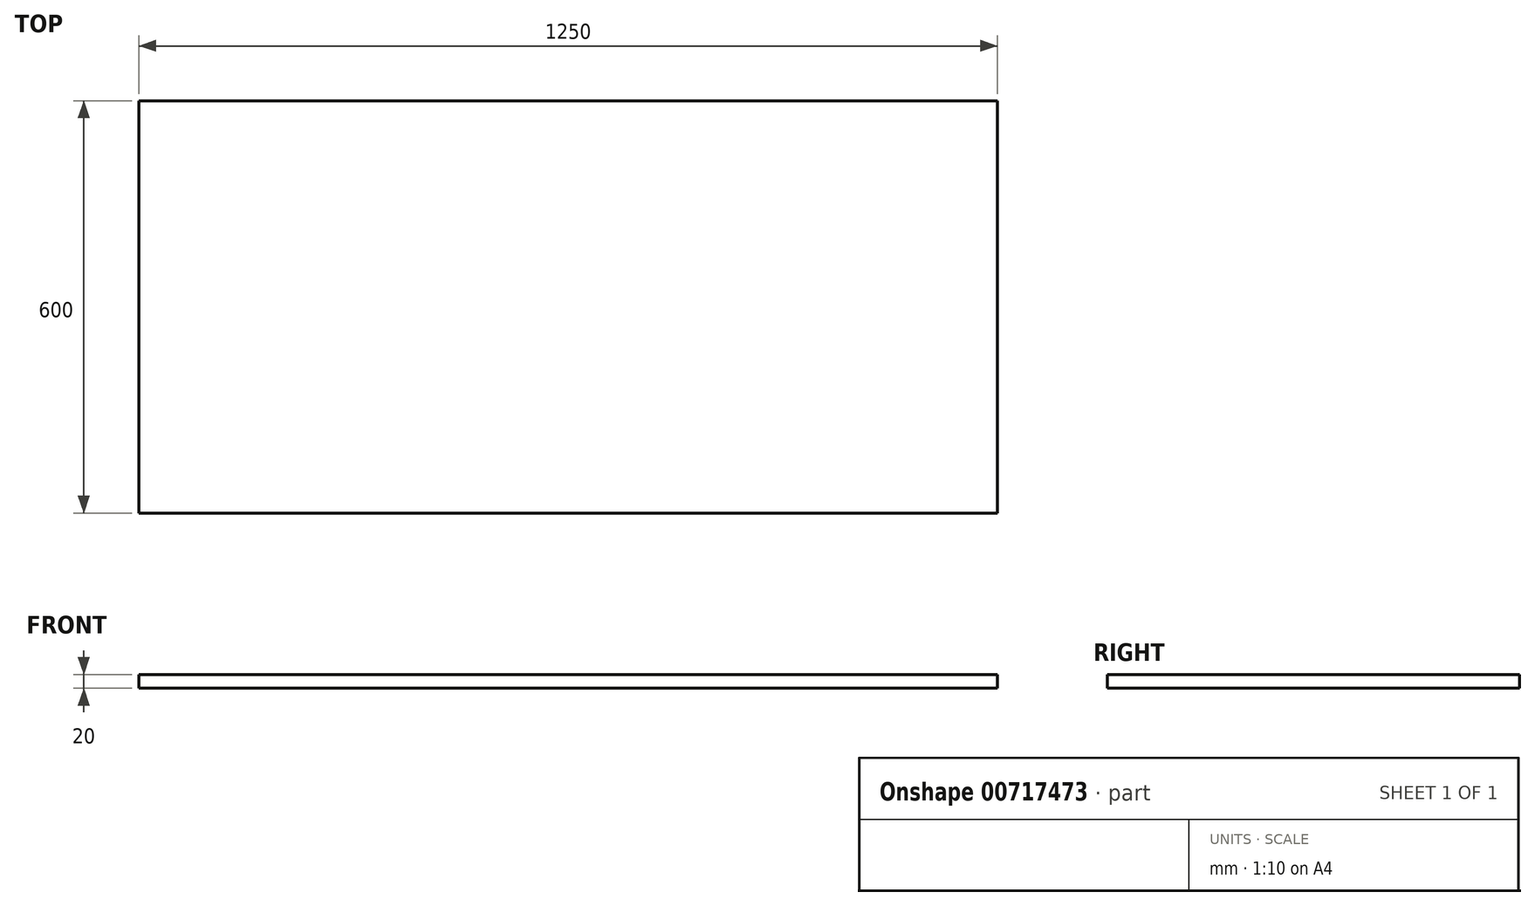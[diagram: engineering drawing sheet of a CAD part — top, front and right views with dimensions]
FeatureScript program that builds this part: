
annotation { "Feature Type Name" : "Feature", "Feature Type Description" : "" }
export const myFeature = defineFeature(function(context is Context, id is Id, definition is map)
    precondition{}
    {
        {
            var Q0;
            Q0=qCreatedBy(makeId("Top.planeOp"),FACE);
            var sketch = newSketch(context, id + "F0", { "sketchPlane" : qUnion([Q0])});
            skLineSegment(sketch, "E0", {"start": v(0, 0) * mm, "end": v(1250, 0) * mm});
            skLineSegment(sketch, "E1", {"start": v(1250, 0) * mm, "end": v(1250, 600) * mm});
            skLineSegment(sketch, "E2", {"start": v(1250, 600) * mm, "end": v(0, 600) * mm});
            skLineSegment(sketch, "E3", {"start": v(0, 600) * mm, "end": v(0, 0) * mm});
            skSolve(sketch);
        }
        {
            var Q0;
            Q0 = qSketchRegion(id + "F0", true);
            extrude(context, id + "F1", {"entities" : qUnion([Q0]), "depth" : 20 * mm, "offsetDistance" : 25 * mm});
        }
    });
